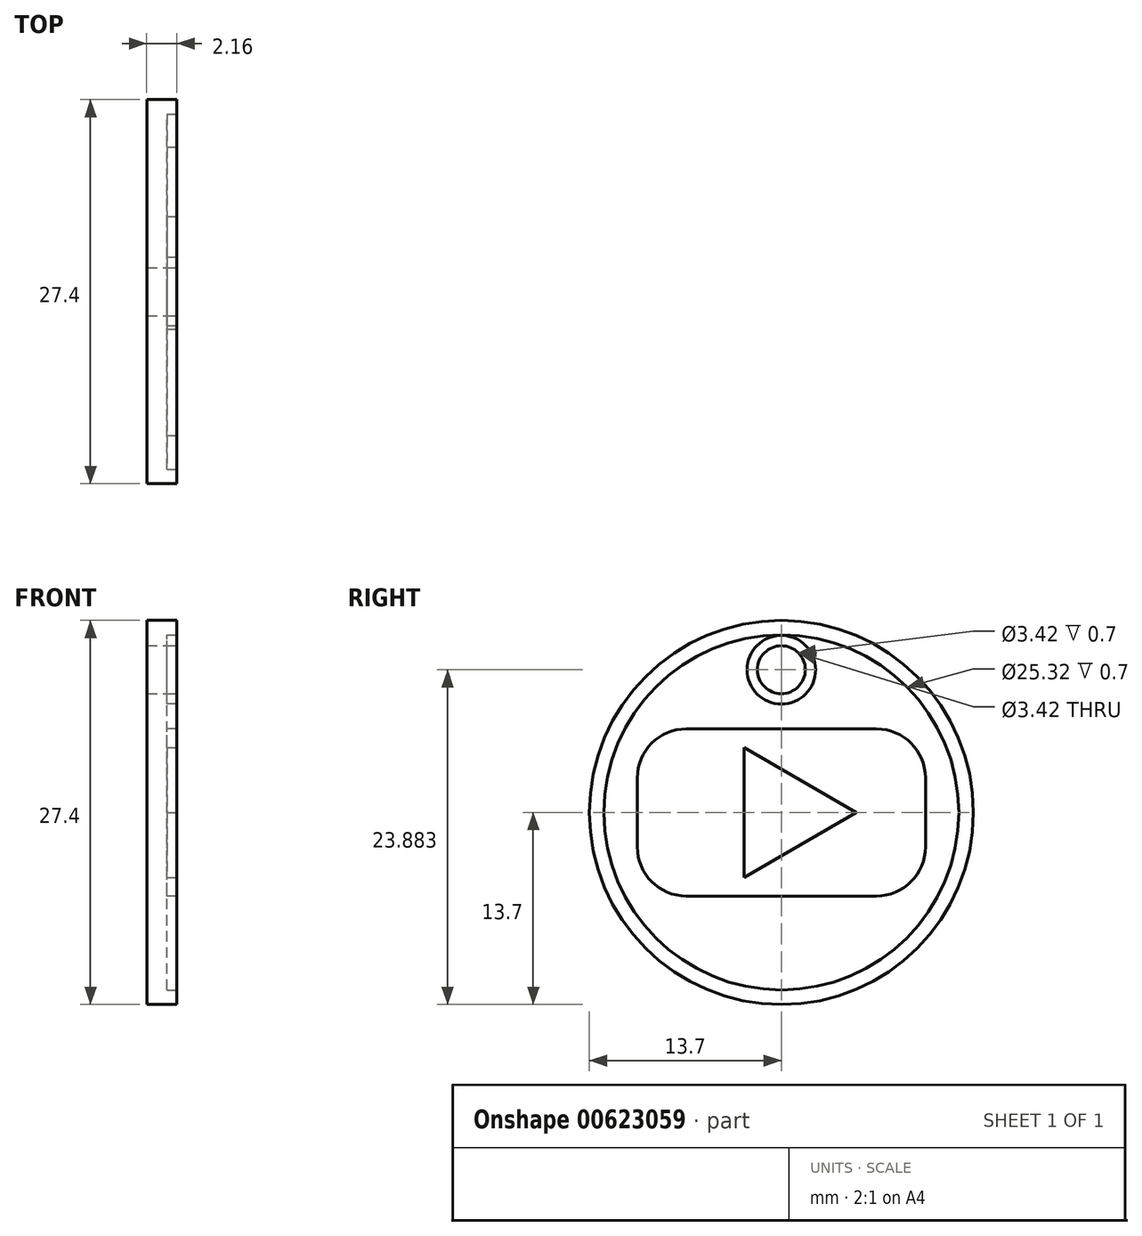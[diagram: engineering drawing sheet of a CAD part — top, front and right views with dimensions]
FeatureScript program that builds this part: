
annotation { "Feature Type Name" : "Feature", "Feature Type Description" : "" }
export const myFeature = defineFeature(function(context is Context, id is Id, definition is map)
    precondition{}
    {
        {
            var Q0;
            Q0=qCreatedBy(makeId("Right.planeOp"),FACE);
            var sketch = newSketch(context, id + "F0", { "sketchPlane" : qUnion([Q0])});
            skCircle(sketch, "E0", {"center": v(0, 0) * mm, "radius": 13.7 * mm});
            skSolve(sketch);
        }
        {
            var Q0;
            Q0=makeQuery(id+"F0.imprint","IMPRINT",FACE,{"disambiguationData":[TD([[makeQuery(id+"F0.imprint","IMPRINT",EDGE,{"derivedFrom":sQuery(id+"F0.wireOp",EDGE,"E0")}),1.0]])]});
            extrude(context, id + "F1", {"entities" : qUnion([Q0]), "endBound" : BoundingType.SYMMETRIC, "depth" : 2.15 * mm, "offsetDistance" : 25 * mm});
        }
        {
            var Q0;
            Q0=makeQuery(id+"F1.opExtrude","CAP_FACE",FACE,{"disambiguationData":[OSD([sQuery(id+"F0.wireOp",EDGE,"E0")])],"isStart":false});
            var sketch = newSketch(context, id + "F2", { "sketchPlane" : qUnion([Q0])});
            skCircle(sketch, "E1", {"center": v(0, 0) * mm, "radius": 12.66 * mm});
            skSolve(sketch);
        }
        {
            var Q0;
            Q0=makeQuery(id+"F2.imprint","IMPRINT",FACE,{"disambiguationData":[TD([[makeQuery(id+"F2.imprint","IMPRINT",EDGE,{"derivedFrom":sQuery(id+"F2.wireOp",EDGE,"E1")}),1.0]])]});
            extrude(context, id + "F3", {"entities" : qUnion([Q0]), "operationType" : NewBodyOperationType.REMOVE, "oppositeDirection" : true, "depth" : 0.7 * mm, "offsetDistance" : 25 * mm});
        }
        {
            var Q0;
            Q0=makeQuery(id+"F3.boolean.opBoolean","COPY",FACE,{"derivedFrom":makeQuery(id+"F3.opExtrude","CAP_FACE",FACE,{"disambiguationData":[OSD([sQuery(id+"F2.wireOp",EDGE,"E1")])],"isStart":false})});
            var sketch = newSketch(context, id + "F4", { "sketchPlane" : qUnion([Q0])});
            skSolve(sketch);
        }
        {
            var Q0;
            Q0=makeQuery(id+"F4.imprint","IMPRINT",FACE,{"disambiguationData":[TD([[makeQuery(id+"F4.imprint","IMPRINT",EDGE,{"derivedFrom":makeQuery(id+"F3.boolean.opBoolean","COPY",EDGE,{"derivedFrom":makeQuery(id+"F3.opExtrude","CAP_EDGE",EDGE,{"disambiguationData":[OSD([sQuery(id+"F2.wireOp",EDGE,"E1")])],"isStart":false})})}),1.0]])]});
            var sketch = newSketch(context, id + "F5", { "sketchPlane" : qUnion([Q0])});
            skCircle(sketch, "E2", {"center": v(0, 10.18) * mm, "radius": 2.45 * mm});
            skSolve(sketch);
        }
        {
            var Q0;
            Q0=makeQuery(id+"F5.imprint","IMPRINT",FACE,{"disambiguationData":[TD([[makeQuery(id+"F5.imprint","IMPRINT",EDGE,{"derivedFrom":sQuery(id+"F5.wireOp",EDGE,"E2")}),1.0]])]});
            extrude(context, id + "F6", {"entities" : qUnion([Q0]), "depth" : 0.7 * mm, "offsetDistance" : 25 * mm});
        }
        {
            var Q0;
            Q0=makeQuery(id+"F6.opExtrude","CAP_FACE",FACE,{"disambiguationData":[OSD([sQuery(id+"F5.wireOp",EDGE,"E2")])],"isStart":false});
            var sketch = newSketch(context, id + "F7", { "sketchPlane" : qUnion([Q0])});
            skCircle(sketch, "E3", {"center": v(0, 10.18) * mm, "radius": 1.71 * mm});
            skSolve(sketch);
        }
        {
            var Q0;
            Q0=makeQuery(id+"F7.imprint","IMPRINT",FACE,{"disambiguationData":[TD([[makeQuery(id+"F7.imprint","IMPRINT",EDGE,{"derivedFrom":sQuery(id+"F7.wireOp",EDGE,"E3")}),1.0]])]});
            extrude(context, id + "F8", {"entities" : qUnion([Q0]), "operationType" : NewBodyOperationType.REMOVE, "endBound" : BoundingType.THROUGH_ALL, "oppositeDirection" : true, "depth" : 25 * mm, "offsetDistance" : 25 * mm});
        }
        {
            var Q0;
            Q0=makeQuery(id+"F4.imprint","IMPRINT",FACE,{"disambiguationData":[TD([[makeQuery(id+"F4.imprint","IMPRINT",EDGE,{"derivedFrom":makeQuery(id+"F3.boolean.opBoolean","COPY",EDGE,{"derivedFrom":makeQuery(id+"F3.opExtrude","CAP_EDGE",EDGE,{"disambiguationData":[OSD([sQuery(id+"F2.wireOp",EDGE,"E1")])],"isStart":false})})}),1.0]])]});
            var sketch = newSketch(context, id + "F9", { "sketchPlane" : qUnion([Q0])});
            skLineSegment(sketch, "E4.left", {"start": v(-9.85, 0.03) * mm, "end": v(-9.85, -0.03) * mm});
            skLineSegment(sketch, "E4.right", {"start": v(9.85, 0.03) * mm, "end": v(9.85, -0.03) * mm});
            skPoint(sketch, "E4.middle", {"position": v(0, 0) * mm});
            skLineSegment(sketch, "E5.bottom", {"start": v(-6.78, 5.96) * mm, "end": v(6.78, 5.96) * mm});
            skLineSegment(sketch, "E5.top", {"start": v(-6.78, -5.96) * mm, "end": v(6.78, -5.96) * mm});
            skLineSegment(sketch, "E5.left", {"start": v(-10.28, 2.46) * mm, "end": v(-10.28, -2.46) * mm});
            skLineSegment(sketch, "E5.right", {"start": v(10.28, 2.46) * mm, "end": v(10.28, -2.46) * mm});
            skPoint(sketch, "E6.visualSharp", {"position": v(10.28, 5.96) * mm});
            skArc(sketch, "E6.filletArc", {"start": v(10.28, 2.46) * mm, "mid": v(9.26, 4.94) * mm, "end": v(6.78, 5.96) * mm});
            skPoint(sketch, "E7.visualSharp", {"position": v(-10.28, 5.96) * mm});
            skArc(sketch, "E7.filletArc", {"start": v(-6.78, 5.96) * mm, "mid": v(-9.26, 4.94) * mm, "end": v(-10.28, 2.46) * mm});
            skPoint(sketch, "E8.visualSharp", {"position": v(-10.28, -5.96) * mm});
            skArc(sketch, "E8.filletArc", {"start": v(-10.28, -2.46) * mm, "mid": v(-9.26, -4.94) * mm, "end": v(-6.78, -5.96) * mm});
            skPoint(sketch, "E9.visualSharp", {"position": v(10.28, -5.96) * mm});
            skArc(sketch, "E9.filletArc", {"start": v(6.78, -5.96) * mm, "mid": v(9.26, -4.94) * mm, "end": v(10.28, -2.46) * mm});
            skSolve(sketch);
        }
        {
            var Q0;
            Q0 = qSketchRegion(id + "F9", true);
            extrude(context, id + "F10", {"entities" : qUnion([Q0]), "operationType" : NewBodyOperationType.ADD, "depth" : 0.7 * mm, "offsetDistance" : 25 * mm});
        }
        {
            var Q0;
            Q0=makeQuery(id+"F10.opExtrude","CAP_FACE",FACE,{"disambiguationData":[OSD([sQuery(id+"F9.wireOp",EDGE,"E5.bottom"),sQuery(id+"F9.wireOp",EDGE,"E5.top"),sQuery(id+"F9.wireOp",EDGE,"E5.left"),sQuery(id+"F9.wireOp",EDGE,"E5.right"),sQuery(id+"F9.wireOp",EDGE,"E6.filletArc"),sQuery(id+"F9.wireOp",EDGE,"E7.filletArc"),sQuery(id+"F9.wireOp",EDGE,"E8.filletArc"),sQuery(id+"F9.wireOp",EDGE,"E9.filletArc")])],"isStart":false});
            var sketch = newSketch(context, id + "F11", { "sketchPlane" : qUnion([Q0])});
            skCircle(sketch, "E10.cCircle", {"center": v(0, 0) * mm, "radius": 2.67 * mm, "construction": true});
            skLineSegment(sketch, "E10.0", {"start": v(-2.67, -4.63) * mm, "end": v(-2.67, 4.63) * mm});
            skLineSegment(sketch, "E10.1", {"start": v(-2.67, 4.63) * mm, "end": v(5.35, 0) * mm});
            skLineSegment(sketch, "E10.2", {"start": v(5.35, 0) * mm, "end": v(-2.67, -4.63) * mm});
            skPoint(sketch, "E10.0.midPoint", {"position": v(-2.67, 0) * mm});
            skSolve(sketch);
        }
        {
            var Q0;
            Q0=makeQuery(id+"F11.imprint","IMPRINT",FACE,{"disambiguationData":[TD([[makeQuery(id+"F11.imprint","IMPRINT",EDGE,{"derivedFrom":sQuery(id+"F11.wireOp",EDGE,"E10.0")}),-1.0]])]});
            extrude(context, id + "F12", {"entities" : qUnion([Q0]), "operationType" : NewBodyOperationType.REMOVE, "oppositeDirection" : true, "depth" : 0.7 * mm, "offsetDistance" : 25 * mm});
        }
    });
